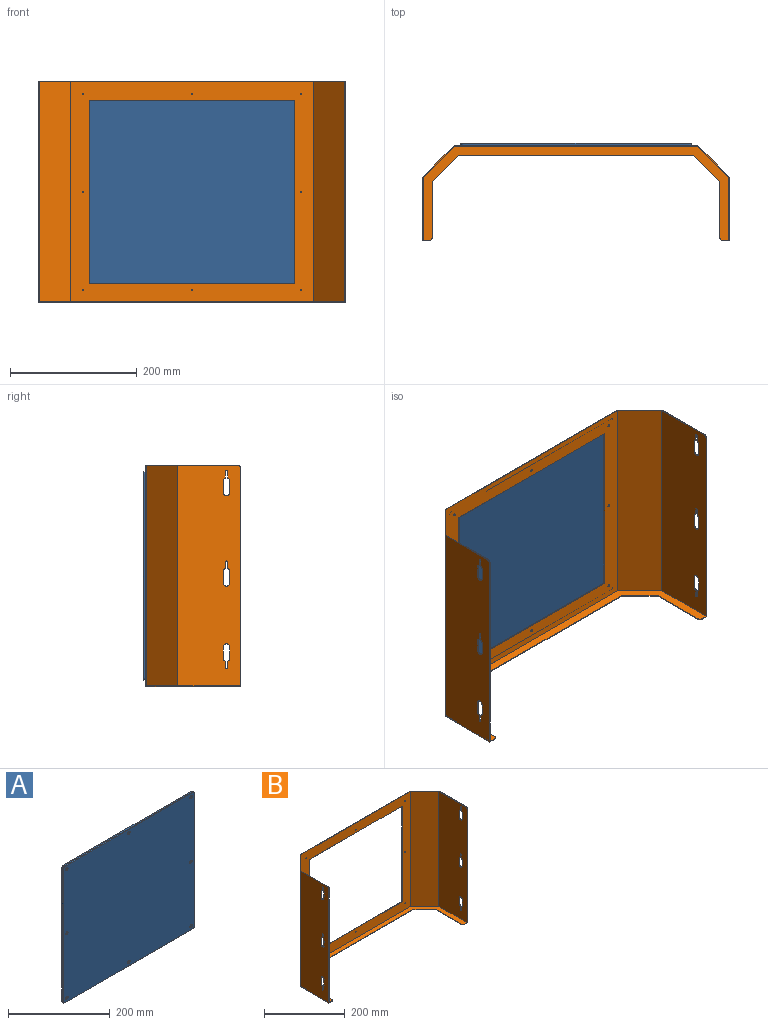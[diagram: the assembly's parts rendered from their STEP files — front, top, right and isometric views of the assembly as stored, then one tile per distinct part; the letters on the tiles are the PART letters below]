
ASSEMBLY  parts=2 mates=1
PART A: 34 faces, bbox 365x4x330 mm
  f0: plane 355x3mm, normal (0,0,-1), area 1065mm2, adj f5,f22,f25,f29
  f1: plane 320x3mm, normal (1,0,0), area 960mm2, adj f5,f22,f23,f26
  f2: plane 355x3mm, normal (0,0,1), area 1065mm2, adj f5,f23,f24,f30
  f3: plane 320x3mm, normal (-1,0,0), area 960mm2, adj f5,f24,f25,f33
  f4: plane 363x328mm, normal (0,-1,0), area 118766.5mm2, adj f7,f9,f11,f13,f15,f17,f19,f21
  f5: plane 365x330mm, normal (0,1,0), area 120355.9mm2, adj f0,f1,f2,f3,f6,f8,f10,f12
  f6: cylinder r=1.7mm len=3.4mm, axis (0,-1,0), area 25mm2, adj f5,f7
  f7: cone r=1.7mm half-angle=45deg, axis (0,-1,0), area 37.3mm2, adj f4,f6
  f8: cylinder r=1.7mm len=3.4mm, axis (0,-1,0), area 25mm2, adj f5,f9
  f9: cone r=1.7mm half-angle=45deg, axis (0,-1,0), area 37.3mm2, adj f4,f8
  f10: cylinder r=1.7mm len=3.4mm, axis (0,-1,0), area 25mm2, adj f5,f11
  f11: cone r=1.7mm half-angle=45deg, axis (0,-1,0), area 37.3mm2, adj f4,f10
  f12: cylinder r=1.7mm len=3.4mm, axis (0,-1,0), area 25mm2, adj f5,f13
  f13: cone r=1.7mm half-angle=45deg, axis (0,-1,0), area 37.3mm2, adj f4,f12
  f14: cylinder r=1.7mm len=3.4mm, axis (0,-1,0), area 25mm2, adj f5,f15
  f15: cone r=1.7mm half-angle=45deg, axis (0,-1,0), area 37.3mm2, adj f4,f14
  f16: cylinder r=1.7mm len=3.4mm, axis (0,-1,0), area 25mm2, adj f5,f17
  f17: cone r=1.7mm half-angle=45deg, axis (0,-1,0), area 37.3mm2, adj f4,f16
  f18: cylinder r=1.7mm len=3.4mm, axis (0,-1,0), area 25mm2, adj f5,f19
  f19: cone r=1.7mm half-angle=45deg, axis (0,-1,0), area 37.3mm2, adj f4,f18
  f20: cylinder r=1.7mm len=3.4mm, axis (0,-1,0), area 25mm2, adj f5,f21
  f21: cone r=1.7mm half-angle=45deg, axis (0,-1,0), area 37.3mm2, adj f4,f20
  f22: cylinder r=5mm len=5mm, axis (0,-1,0), area 23.6mm2, adj f0,f1,f5,f27
  f23: cylinder r=5mm len=5mm, axis (0,1,0), area 23.6mm2, adj f1,f2,f5,f28
  f24: cylinder r=5mm len=5mm, axis (0,-1,0), area 23.6mm2, adj f2,f3,f5,f32
  f25: cylinder r=5mm len=5mm, axis (0,1,0), area 23.6mm2, adj f0,f3,f5,f31
  f26: plane 320x1mm, normal (0.71,-0.71,0), area 452.5mm2, adj f1,f4,f27,f28
  f27: cone r=4mm half-angle=45deg, axis (0,1,0), area 10mm2, adj f4,f22,f26,f29
  f28: cone r=4mm half-angle=45deg, axis (0,1,0), area 10mm2, adj f4,f23,f26,f30
  f29: plane 355x1mm, normal (0,-0.71,-0.71), area 502mm2, adj f0,f4,f27,f31
  f30: plane 355x1mm, normal (0,-0.71,0.71), area 502mm2, adj f2,f4,f28,f32
  f31: cone r=4mm half-angle=45deg, axis (0,1,0), area 10mm2, adj f4,f25,f29,f33
  f32: cone r=4mm half-angle=45deg, axis (0,1,0), area 10mm2, adj f4,f24,f30,f33
  f33: plane 320x1mm, normal (-0.71,-0.71,0), area 452.5mm2, adj f3,f4,f31,f32
PART B: 84 faces, bbox 485x150x350 mm
  f0: plane 345x10mm, normal (0,-1,0), area 424.6mm2, adj f4,f8,f11,f14,f81,f83
  f1: plane 485x145mm, normal (0,0,1), area 857.3mm2, adj f2,f3,f4,f6,f7,f9,f10,f11
  f2: plane 385x350mm, normal (0,1,0), area 40460.7mm2, adj f1,f3,f7,f8,f20,f21,f22,f23
  f3: plane 350x50mm, normal (-0.71,0.71,0), area 24748.7mm2, adj f1,f2,f4,f8
  f4: plane 350x100mm, normal (-1,0,0), area 34098.5mm2, adj f0,f1,f3,f8,f56,f57,f58,f59
  f5: plane 345x10mm, normal (0,-1,0), area 424.6mm2, adj f6,f8,f12,f14,f80,f82
  f6: plane 350x100mm, normal (1,0,0), area 34098.5mm2, adj f1,f5,f7,f8,f32,f33,f34,f35
  f7: plane 350x50mm, normal (0.71,0.71,0), area 24748.7mm2, adj f1,f2,f6,f8
  f8: plane 485x150mm, normal (0,0,-1), area 10512.8mm2, adj f0,f2,f3,f4,f5,f6,f7,f15
  f9: plane 384.01x348.8mm, normal (0,-1,0), area 39652mm2, adj f1,f10,f13,f14,f20,f21,f22,f23
  f10: plane 348.8x49.3mm, normal (0.71,-0.71,0), area 24317.1mm2, adj f1,f9,f11,f14
  f11: plane 348.8x99.5mm, normal (1,0,0), area 33805.1mm2, adj f0,f1,f10,f14,f56,f57,f58,f59
  f12: plane 348.8x99.5mm, normal (-1,0,0), area 33805.1mm2, adj f1,f5,f13,f14,f32,f33,f34,f35
  f13: plane 348.8x49.3mm, normal (-0.71,-0.71,0), area 24317.1mm2, adj f1,f9,f12,f14
  f14: plane 482.6x148.8mm, normal (0,0,1), area 9643.5mm2, adj f0,f5,f9,f10,f11,f12,f13,f15
  f15: plane 88.79x1.2mm, normal (1,0,0), area 106.5mm2, adj f8,f14,f16,f81
  f16: plane 41.21x41.21mm, normal (0.71,-0.71,0), area 69.9mm2, adj f8,f14,f15,f17
  f17: plane 372.57x1.2mm, normal (0,-1,0), area 447.1mm2, adj f8,f14,f16,f19
  f18: plane 88.79x1.2mm, normal (-1,0,0), area 106.5mm2, adj f8,f14,f19,f80
  f19: plane 41.21x41.21mm, normal (-0.71,-0.71,0), area 69.9mm2, adj f8,f14,f17,f18
  f20: plane 290x1.2mm, normal (-1,0,0), area 348mm2, adj f2,f9,f21,f22
  f21: plane 325x1.2mm, normal (0,0,-1), area 390mm2, adj f2,f9,f20,f23
  f22: plane 325x1.2mm, normal (0,0,1), area 390mm2, adj f2,f9,f20,f23
  f23: plane 290x1.2mm, normal (1,0,0), area 348mm2, adj f2,f9,f21,f22
  f24: cylinder r=1.25mm len=2.5mm, axis (0,1,0), area 9.4mm2, adj f2,f9
  f25: cylinder r=1.25mm len=2.5mm, axis (0,1,0), area 9.4mm2, adj f2,f9
  f26: cylinder r=1.25mm len=2.5mm, axis (0,1,0), area 9.4mm2, adj f2,f9
  f27: cylinder r=1.25mm len=2.5mm, axis (0,1,0), area 9.4mm2, adj f2,f9
  f28: cylinder r=1.25mm len=2.5mm, axis (0,1,0), area 9.4mm2, adj f2,f9
  f29: cylinder r=1.25mm len=2.5mm, axis (0,1,0), area 9.4mm2, adj f2,f9
  f30: cylinder r=1.25mm len=2.5mm, axis (0,1,0), area 9.4mm2, adj f2,f9
  f31: cylinder r=1.25mm len=2.5mm, axis (0,1,0), area 9.4mm2, adj f2,f9
  f32: cylinder r=1.75mm len=3.5mm, axis (-1,0,0), area 6.6mm2, adj f6,f12,f33,f39
  f33: plane 10.32x1.2mm, normal (0,1,0), area 12.4mm2, adj f6,f12,f32,f34
  f34: cylinder r=5mm len=4.68mm, axis (-1,0,0), area 7.3mm2, adj f6,f12,f33,f35
  f35: plane 18x1.2mm, normal (0,1,0), area 21.6mm2, adj f6,f12,f34,f36
  f36: cylinder r=5mm len=10mm, axis (-1,0,0), area 18.8mm2, adj f6,f12,f35,f37
  f37: plane 18x1.2mm, normal (0,-1,0), area 21.6mm2, adj f6,f12,f36,f38
  f38: cylinder r=5mm len=4.68mm, axis (-1,0,0), area 7.3mm2, adj f6,f12,f37,f39
  f39: plane 10.32x1.2mm, normal (0,-1,0), area 12.4mm2, adj f6,f12,f32,f38
  f40: cylinder r=1.75mm len=3.5mm, axis (-1,0,0), area 6.6mm2, adj f6,f12,f41,f47
  f41: plane 10.32x1.2mm, normal (0,-1,0), area 12.4mm2, adj f6,f12,f40,f42
  f42: cylinder r=5mm len=4.68mm, axis (-1,0,0), area 7.3mm2, adj f6,f12,f41,f43
  f43: plane 18x1.2mm, normal (0,-1,0), area 21.6mm2, adj f6,f12,f42,f44
  f44: cylinder r=5mm len=10mm, axis (-1,0,0), area 18.8mm2, adj f6,f12,f43,f45
  f45: plane 18x1.2mm, normal (0,1,0), area 21.6mm2, adj f6,f12,f44,f46
  f46: cylinder r=5mm len=4.68mm, axis (-1,0,0), area 7.3mm2, adj f6,f12,f45,f47
  f47: plane 10.32x1.2mm, normal (0,1,0), area 12.4mm2, adj f6,f12,f40,f46
  f48: cylinder r=1.75mm len=3.5mm, axis (-1,0,0), area 6.6mm2, adj f6,f12,f49,f55
  f49: plane 10.32x1.2mm, normal (0,1,0), area 12.4mm2, adj f6,f12,f48,f50
  f50: cylinder r=5mm len=4.68mm, axis (-1,0,0), area 7.3mm2, adj f6,f12,f49,f51
  f51: plane 18x1.2mm, normal (0,1,0), area 21.6mm2, adj f6,f12,f50,f52
  f52: cylinder r=5mm len=10mm, axis (-1,0,0), area 18.8mm2, adj f6,f12,f51,f53
  f53: plane 18x1.2mm, normal (0,-1,0), area 21.6mm2, adj f6,f12,f52,f54
  f54: cylinder r=5mm len=4.68mm, axis (-1,0,0), area 7.3mm2, adj f6,f12,f53,f55
  f55: plane 10.32x1.2mm, normal (0,-1,0), area 12.4mm2, adj f6,f12,f48,f54
  f56: plane 10.32x1.2mm, normal (0,-1,0), area 12.4mm2, adj f4,f11,f57,f63
  f57: cylinder r=5mm len=4.68mm, axis (-1,0,0), area 7.3mm2, adj f4,f11,f56,f58
  f58: plane 18x1.2mm, normal (0,-1,0), area 21.6mm2, adj f4,f11,f57,f59
  f59: cylinder r=5mm len=10mm, axis (-1,0,0), area 18.8mm2, adj f4,f11,f58,f60
  f60: plane 18x1.2mm, normal (0,1,0), area 21.6mm2, adj f4,f11,f59,f61
  f61: cylinder r=5mm len=4.68mm, axis (-1,0,0), area 7.3mm2, adj f4,f11,f60,f62
  f62: plane 10.32x1.2mm, normal (0,1,0), area 12.4mm2, adj f4,f11,f61,f63
  f63: cylinder r=1.75mm len=3.5mm, axis (-1,0,0), area 6.6mm2, adj f4,f11,f56,f62
  f64: plane 10.32x1.2mm, normal (0,1,0), area 12.4mm2, adj f4,f11,f65,f71
  f65: cylinder r=5mm len=4.68mm, axis (-1,0,0), area 7.3mm2, adj f4,f11,f64,f66
  f66: plane 18x1.2mm, normal (0,1,0), area 21.6mm2, adj f4,f11,f65,f67
  f67: cylinder r=5mm len=10mm, axis (-1,0,0), area 18.8mm2, adj f4,f11,f66,f68
  f68: plane 18x1.2mm, normal (0,-1,0), area 21.6mm2, adj f4,f11,f67,f69
  f69: cylinder r=5mm len=4.68mm, axis (-1,0,0), area 7.3mm2, adj f4,f11,f68,f70
  f70: plane 10.32x1.2mm, normal (0,-1,0), area 12.4mm2, adj f4,f11,f69,f71
  f71: cylinder r=1.75mm len=3.5mm, axis (-1,0,0), area 6.6mm2, adj f4,f11,f64,f70
  f72: plane 10.32x1.2mm, normal (0,-1,0), area 12.4mm2, adj f4,f11,f73,f79
  f73: cylinder r=5mm len=4.68mm, axis (-1,0,0), area 7.3mm2, adj f4,f11,f72,f74
  f74: plane 18x1.2mm, normal (0,-1,0), area 21.6mm2, adj f4,f11,f73,f75
  f75: cylinder r=5mm len=10mm, axis (-1,0,0), area 18.8mm2, adj f4,f11,f74,f76
  f76: plane 18x1.2mm, normal (0,1,0), area 21.6mm2, adj f4,f11,f75,f77
  f77: cylinder r=5mm len=4.68mm, axis (-1,0,0), area 7.3mm2, adj f4,f11,f76,f78
  f78: plane 10.32x1.2mm, normal (0,1,0), area 12.4mm2, adj f4,f11,f77,f79
  f79: cylinder r=1.75mm len=3.5mm, axis (-1,0,0), area 6.6mm2, adj f4,f11,f72,f78
  f80: cylinder r=5mm len=5mm, axis (0,0,1), area 9.4mm2, adj f5,f8,f14,f18
  f81: cylinder r=5mm len=5mm, axis (0,0,-1), area 9.4mm2, adj f0,f8,f14,f15
  f82: cylinder r=5mm len=5mm, axis (-1,0,0), area 9.4mm2, adj f1,f5,f6,f12
  f83: cylinder r=5mm len=5mm, axis (-1,0,0), area 9.4mm2, adj f0,f1,f4,f11
PLACE A rot(axis=(0,0,1),180deg) t=(-0.87,74.61,-4.84)mm
PLACE B t=(8.35,74.6,-179.84)mm
MATE fastened A.f16 <-> B.f24  axis (0,-1,0) through (171.63,74.61,150.16)mm
